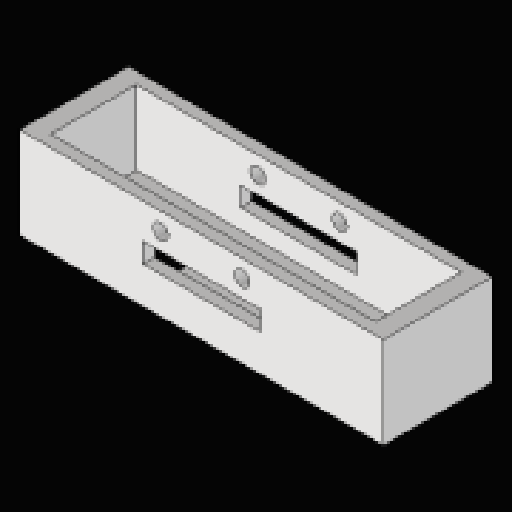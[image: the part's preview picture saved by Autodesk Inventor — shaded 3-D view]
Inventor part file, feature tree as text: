
AUTODESK INVENTOR PART (.ipt)
format: ipt  version: 2023.2 (Build 272271030, 271C)  size: 192,000 bytes
history: native  units: mm
features: sketch x6, extrude x5, projected_geometry x5, reference x4, other x4, hole x1
ambient origin geometry x8: Origin, YZ Plane, XZ Plane, XY Plane, X Axis, Y Axis, Z Axis, Center Point
bodies: Solid1 (feature_tree)
feature tree (25):
  extrude  "Extrusion1"  Depth=100.0mm
  extrude  "Extrusion2"  Depth=3.0mm
  extrude  "Extrusion3"  Depth=7.65mm
  hole  "Hole1"  [1 undecoded]
  extrude  "Extrusion4"  Depth=12.7mm
  extrude  "Extrusion5"  Depth=7.65mm
  sketch  "Sketch1"  dims[d0=93.4mm d1=100.0mm]
  sketch  "Sketch2"  dims[d2=3.0mm d3=0.0mm d4=3.0mm]
  projected_geometry  "Projected Loop1"
  reference  "Reference1"
  reference  "Reference2"
  reference  "Reference3"
  reference  "Reference4"
  sketch  "Sketch3"  dims[d6=9.8mm d7=7.65mm]
  projected_geometry  "Projected Loop2"
  sketch  "Sketch4"  dims[d8=23.0mm d9=9.8mm]
  projected_geometry  "Projected Loop3"
  sketch  "Sketch5"  dims[d11=4.5mm d12=0.0mm d13=12.7mm]
  projected_geometry  "Projected Loop4"
  sketch  "Sketch6"  dims[d14=28.0mm d15=7.65mm d16=2.5mm d17=5.0mm d18=5.0mm d19=22.0mm d20=19.0mm d21=0.0mm d23=36.2mm d24=36.2mm d25=4.55mm d26=4.0mm d27=6.0mm d28=8.0mm d29=8.0mm d30=90.0deg d31=8.0mm d32=20.594885mm d33=9.0mm d34=14.0mm d35=30.0mm d36=0.0mm d37=0.0mm d38=10.0mm d39=0.0mm]
  projected_geometry  "Projected Loop5"
  other  "<userpath>\OneDrive\Documents\Arduino\Onslaught\CAD\Frame Test\Frame Test.iam"
  other  "Frame Test.iam"
  other  "SG90 - Micro Servo 9g - Tower Pro:2"
  other  "SG90 - Micro Servo 9g - Tower Pro:1"
note: 1 required parameter value undecoded (feature->parameter linkage not recoverable at this tier; creation-order binding heuristic only, values carry confidence <= 0.55)
